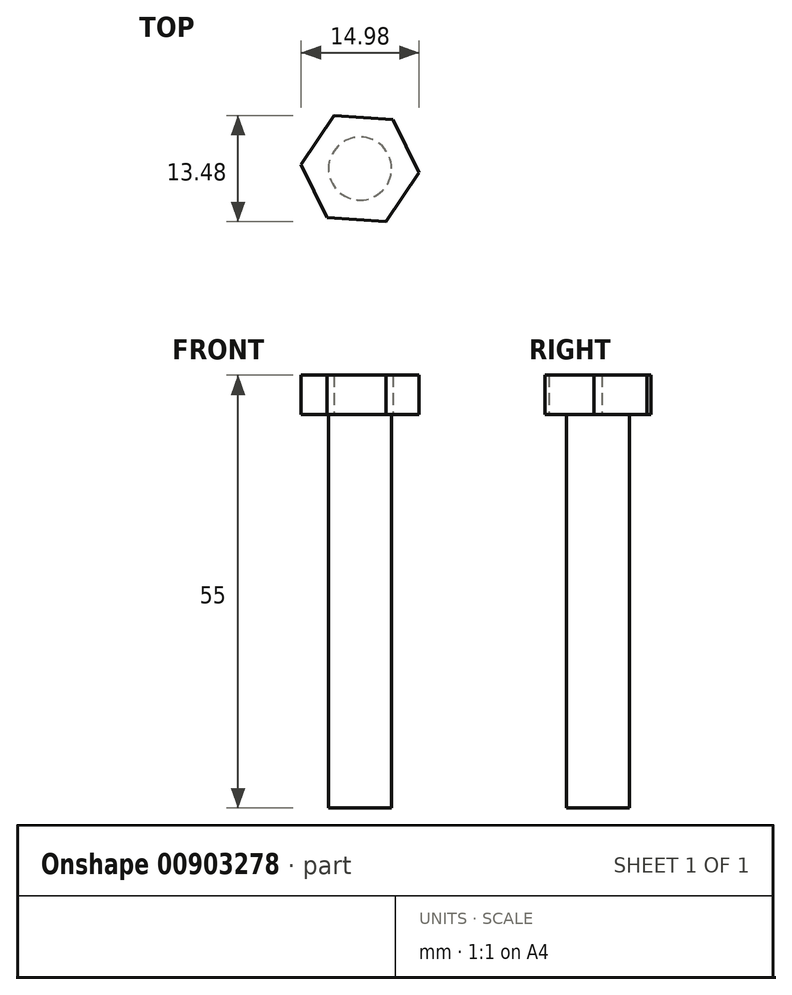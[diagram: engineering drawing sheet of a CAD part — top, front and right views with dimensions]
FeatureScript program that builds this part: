
annotation { "Feature Type Name" : "Feature", "Feature Type Description" : "" }
export const myFeature = defineFeature(function(context is Context, id is Id, definition is map)
    precondition{}
    {
        {
            var Q0;
            Q0=qCreatedBy(makeId("Top.planeOp"),FACE);
            var sketch = newSketch(context, id + "F0", { "sketchPlane" : qUnion([Q0])});
            skCircle(sketch, "E0", {"center": v(23.02, -36.6) * mm, "radius": 4 * mm});
            skCircle(sketch, "E1", {"center": v(0, 0) * mm, "radius": 4 * mm});
            skSolve(sketch);
        }
        {
            var Q0;
            Q0=makeQuery(id+"F0.imprint","IMPRINT",FACE,{"disambiguationData":[TD([[makeQuery(id+"F0.imprint","IMPRINT",EDGE,{"derivedFrom":sQuery(id+"F0.wireOp",EDGE,"E1")}),1.0]])]});
            extrude(context, id + "F1", {"entities" : qUnion([Q0]), "depth" : 50 * mm, "offsetDistance" : 25 * mm});
        }
        {
            var Q0;
            Q0=makeQuery(id+"F1.opExtrude","CAP_FACE",FACE,{"disambiguationData":[OSD([sQuery(id+"F0.wireOp",EDGE,"E1")])],"isStart":false});
            var sketch = newSketch(context, id + "F2", { "sketchPlane" : qUnion([Q0])});
            skCircle(sketch, "E2.cCircle", {"center": v(0, 0) * mm, "radius": 6.5 * mm, "construction": true});
            skLineSegment(sketch, "E2.0", {"start": v(7.49, -0.52) * mm, "end": v(3.3, -6.74) * mm});
            skLineSegment(sketch, "E2.1", {"start": v(3.3, -6.74) * mm, "end": v(-4.2, -6.23) * mm});
            skLineSegment(sketch, "E2.2", {"start": v(-4.2, -6.23) * mm, "end": v(-7.49, 0.52) * mm});
            skLineSegment(sketch, "E2.3", {"start": v(-7.49, 0.52) * mm, "end": v(-3.3, 6.74) * mm});
            skLineSegment(sketch, "E2.4", {"start": v(-3.3, 6.74) * mm, "end": v(4.2, 6.23) * mm});
            skLineSegment(sketch, "E2.5", {"start": v(4.2, 6.23) * mm, "end": v(7.49, -0.52) * mm});
            skPoint(sketch, "E2.0.midPoint", {"position": v(5.4, -3.63) * mm});
            skSolve(sketch);
        }
        {
            var Q0;
            Q0=makeQuery(id+"F2.imprint","IMPRINT",FACE,{"disambiguationData":[TD([[makeQuery(id+"F2.imprint","IMPRINT",EDGE,{"derivedFrom":sQuery(id+"F2.wireOp",EDGE,"E2.0")}),-1.0]])]});
            var Q1;
            Q1=makeQuery(id+"F2.imprint","IMPRINT",FACE,{"disambiguationData":[TD([[makeQuery(id+"F2.imprint","IMPRINT",EDGE,{"derivedFrom":makeQuery(id+"F1.opExtrude","CAP_EDGE",EDGE,{"disambiguationData":[OSD([sQuery(id+"F0.wireOp",EDGE,"E1")])],"isStart":false})}),1.0]])]});
            extrude(context, id + "F3", {"entities" : qUnion([Q0, Q1]), "operationType" : NewBodyOperationType.ADD, "depth" : 5 * mm, "offsetDistance" : 25 * mm});
        }
    });
